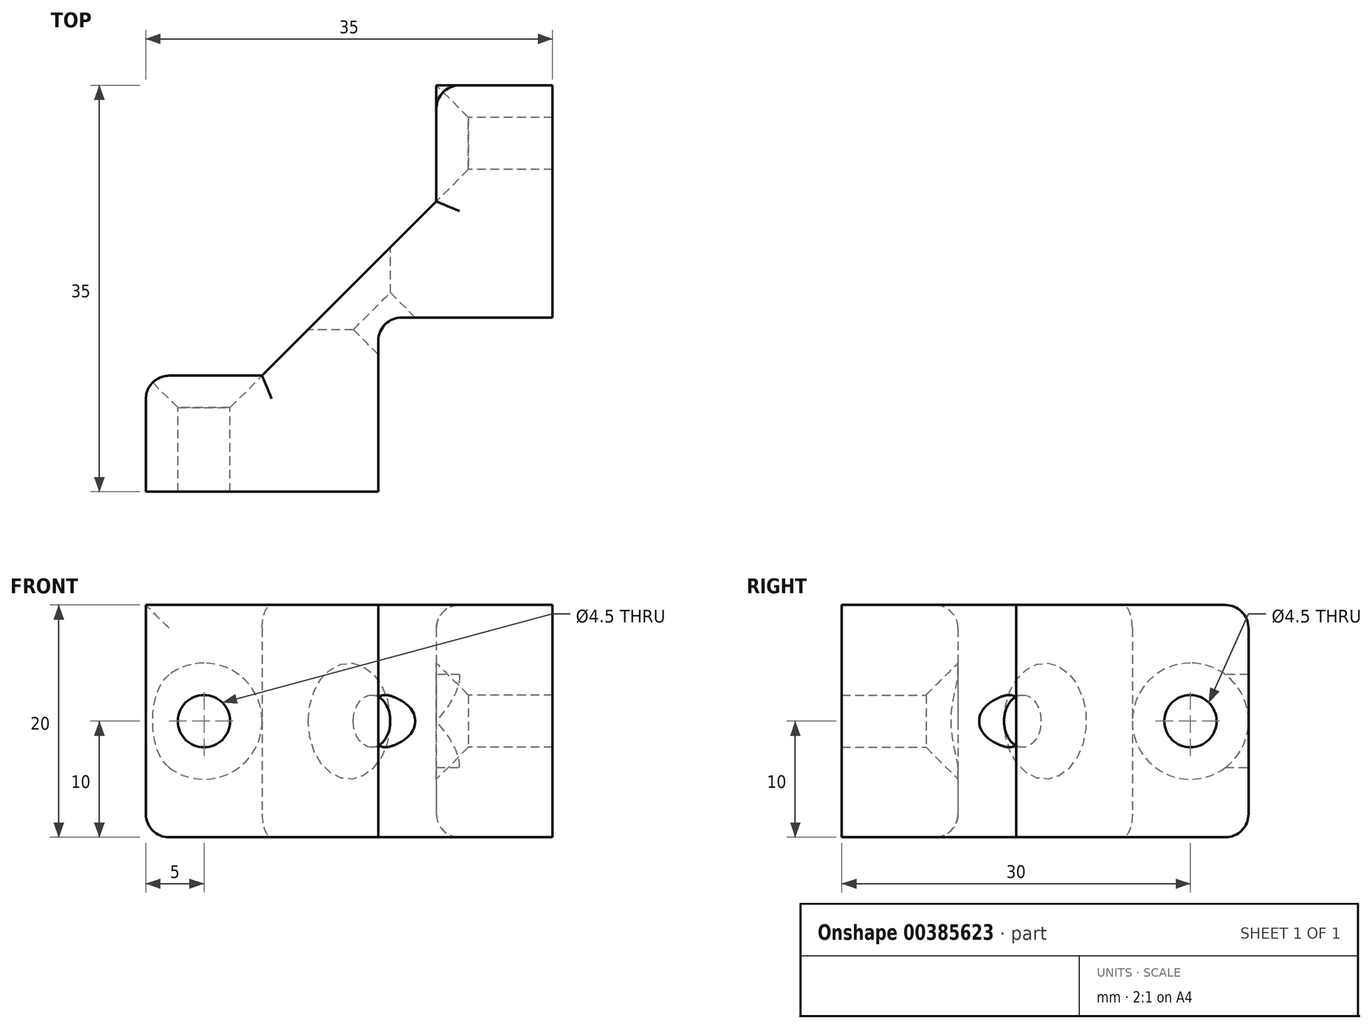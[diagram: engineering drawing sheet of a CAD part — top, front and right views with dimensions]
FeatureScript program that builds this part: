
annotation { "Feature Type Name" : "Feature", "Feature Type Description" : "" }
export const myFeature = defineFeature(function(context is Context, id is Id, definition is map)
    precondition{}
    {
        {
            var Q0;
            Q0=qCreatedBy(makeId("Top.planeOp"),FACE);
            var sketch = newSketch(context, id + "F0", { "sketchPlane" : qUnion([Q0])});
            skLineSegment(sketch, "E0", {"start": v(2, 0) * mm, "end": v(15, 0) * mm});
            skLineSegment(sketch, "E1", {"start": v(15, 0) * mm, "end": v(15, 20) * mm});
            skLineSegment(sketch, "E2", {"start": v(15, 20) * mm, "end": v(5, 20) * mm});
            skLineSegment(sketch, "E3", {"start": v(5, 20) * mm, "end": v(5, 10) * mm});
            skLineSegment(sketch, "E4", {"start": v(5, 10) * mm, "end": v(-10, -5) * mm});
            skLineSegment(sketch, "E5", {"start": v(-10, -5) * mm, "end": v(-20, -5) * mm});
            skLineSegment(sketch, "E6", {"start": v(-20, -5) * mm, "end": v(-20, -15) * mm});
            skLineSegment(sketch, "E7", {"start": v(-20, -15) * mm, "end": v(0, -15) * mm});
            skLineSegment(sketch, "E8", {"start": v(0, -15) * mm, "end": v(0, -2) * mm});
            skPoint(sketch, "E9.visualSharp", {"position": v(0, 0) * mm});
            skArc(sketch, "E9.filletArc", {"start": v(2, 0) * mm, "mid": v(0.59, -0.59) * mm, "end": v(0, -2) * mm});
            skSolve(sketch);
        }
        {
            var Q0;
            Q0 = qSketchRegion(id + "F0", true);
            extrude(context, id + "F1", {"entities" : qUnion([Q0]), "depth" : 20 * mm});
        }
        {
            var Q0;
            Q0=makeQuery(id+"F1.opExtrude","SWEPT_FACE",FACE,{"disambiguationData":[OSD([sQuery(id+"F0.wireOp",EDGE,"E5")])]});
            var sketch = newSketch(context, id + "F2", { "sketchPlane" : qUnion([Q0])});
            skCircle(sketch, "E10", {"center": v(15, 10) * mm, "radius": 2.5 * mm});
            skSolve(sketch);
        }
        {
            var Q0;
            Q0=sQuery(id+"F2.wireOp",VERTEX,"E10.center");
            var Q1;
            Q1=makeQuery(id+"F1.opExtrude","SWEPT_BODY",BODY,{"disambiguationData":[OSD([sQuery(id+"F0.wireOp",EDGE,"E0"),sQuery(id+"F0.wireOp",EDGE,"E1"),sQuery(id+"F0.wireOp",EDGE,"E2"),sQuery(id+"F0.wireOp",EDGE,"E3"),sQuery(id+"F0.wireOp",EDGE,"E4"),sQuery(id+"F0.wireOp",EDGE,"E5"),sQuery(id+"F0.wireOp",EDGE,"E6"),sQuery(id+"F0.wireOp",EDGE,"E7"),sQuery(id+"F0.wireOp",EDGE,"E8"),sQuery(id+"F0.wireOp",EDGE,"E9.filletArc")])]});
            hole(context, id + "F3", {"style" : HoleStyle.C_SINK, "endStyle" : HoleEndStyle.THROUGH, "holeDiameter" : 4.5 * mm, "cSinkDiameter" : 10 * mm, "cSinkAngle" : 90 * degree, "isTappedThrough" : true, "tappedDepth" : 12.7 * mm, "tapClearance" : 3, "startFromSketch" : true, "locations" : qUnion([Q0]), "scope" : qUnion([Q1])});
        }
        {
            var Q0;
            Q0=makeQuery(id+"F1.opExtrude","SWEPT_FACE",FACE,{"disambiguationData":[OSD([sQuery(id+"F0.wireOp",EDGE,"E3")])]});
            var sketch = newSketch(context, id + "F4", { "sketchPlane" : qUnion([Q0])});
            skCircle(sketch, "E11", {"center": v(-15, 10) * mm, "radius": 2 * mm});
            skSolve(sketch);
        }
        {
            var Q0;
            Q0=sQuery(id+"F4.wireOp",VERTEX,"E11.center");
            var Q1;
            Q1=makeQuery(id+"F1.opExtrude","SWEPT_BODY",BODY,{"disambiguationData":[OSD([sQuery(id+"F0.wireOp",EDGE,"E0"),sQuery(id+"F0.wireOp",EDGE,"E1"),sQuery(id+"F0.wireOp",EDGE,"E2"),sQuery(id+"F0.wireOp",EDGE,"E3"),sQuery(id+"F0.wireOp",EDGE,"E4"),sQuery(id+"F0.wireOp",EDGE,"E5"),sQuery(id+"F0.wireOp",EDGE,"E6"),sQuery(id+"F0.wireOp",EDGE,"E7"),sQuery(id+"F0.wireOp",EDGE,"E8"),sQuery(id+"F0.wireOp",EDGE,"E9.filletArc")])]});
            hole(context, id + "F5", {"style" : HoleStyle.C_SINK, "endStyle" : HoleEndStyle.THROUGH, "holeDiameter" : 4.5 * mm, "cSinkDiameter" : 10 * mm, "cSinkAngle" : 90 * degree, "isTappedThrough" : true, "tappedDepth" : 12.7 * mm, "tapClearance" : 3, "startFromSketch" : true, "locations" : qUnion([Q0]), "scope" : qUnion([Q1])});
        }
        {
            var Q0;
            Q0=makeQuery(id+"F1.opExtrude","CAP_EDGE",EDGE,{"disambiguationData":[OSD([sQuery(id+"F0.wireOp",EDGE,"E4")])],"isStart":false});
            fillet(context, id + "F6", {"entities" : qUnion([Q0]), "radius" : 2 * mm, "tangentPropagation" : true, "allowEdgeOverflow" : false});
        }
        {
            var Q0;
            Q0=makeQuery(id+"F1.opExtrude","CAP_EDGE",EDGE,{"disambiguationData":[OSD([sQuery(id+"F0.wireOp",EDGE,"E3")])],"isStart":false});
            fillet(context, id + "F7", {"entities" : qUnion([Q0]), "radius" : 2 * mm, "tangentPropagation" : true, "allowEdgeOverflow" : false});
        }
        {
            var Q0;
            Q0=makeQuery(id+"F1.opExtrude","CAP_EDGE",EDGE,{"disambiguationData":[OSD([sQuery(id+"F0.wireOp",EDGE,"E5")])],"isStart":false});
            fillet(context, id + "F8", {"entities" : qUnion([Q0]), "radius" : 2 * mm, "tangentPropagation" : true, "allowEdgeOverflow" : false});
        }
        {
            var Q0;
            Q0=makeQuery(id+"F1.opExtrude","CAP_EDGE",EDGE,{"disambiguationData":[OSD([sQuery(id+"F0.wireOp",EDGE,"E3")])],"isStart":true});
            fillet(context, id + "F9", {"entities" : qUnion([Q0]), "radius" : 2 * mm, "tangentPropagation" : true, "allowEdgeOverflow" : false});
        }
        {
            var Q0;
            Q0=makeQuery(id+"F1.opExtrude","CAP_EDGE",EDGE,{"disambiguationData":[OSD([sQuery(id+"F0.wireOp",EDGE,"E4")])],"isStart":true});
            var Q1;
            Q1=makeQuery(id+"F1.opExtrude","CAP_EDGE",EDGE,{"disambiguationData":[OSD([sQuery(id+"F0.wireOp",EDGE,"E5")])],"isStart":true});
            fillet(context, id + "F10", {"entities" : qUnion([Q0, Q1]), "radius" : 2 * mm, "tangentPropagation" : true, "allowEdgeOverflow" : false});
        }
        {
            var Q0;
            Q0=makeQuery(id+"F1.opExtrude","CAP_EDGE",EDGE,{"disambiguationData":[OSD([sQuery(id+"F0.wireOp",EDGE,"E6")])],"isStart":true});
            fillet(context, id + "F11", {"entities" : qUnion([Q0]), "radius" : 2 * mm, "tangentPropagation" : true, "allowEdgeOverflow" : false});
        }
        {
            var Q0;
            {var subQ0=sQuery(id+"F0.wireOp",EDGE,"E3");var subQ1=sQuery(id+"F0.wireOp",EDGE,"E2");Q0=makeQuery(id+"F5.hole-0.boolean.opBoolean","SPLIT",EDGE,{"disambiguationData":[TD([makeQuery(id+"F1.opExtrude","CAP_FACE",FACE,{"disambiguationData":[OSD([sQuery(id+"F0.wireOp",EDGE,"E0"),sQuery(id+"F0.wireOp",EDGE,"E1"),subQ1,subQ0,sQuery(id+"F0.wireOp",EDGE,"E4"),sQuery(id+"F0.wireOp",EDGE,"E5"),sQuery(id+"F0.wireOp",EDGE,"E6"),sQuery(id+"F0.wireOp",EDGE,"E7"),sQuery(id+"F0.wireOp",EDGE,"E8"),sQuery(id+"F0.wireOp",EDGE,"E9.filletArc")])],"isStart":false})])],"derivedFrom":makeQuery(id+"F1.opExtrude","SWEPT_EDGE",EDGE,{"disambiguationData":[OSD([subQ1,subQ0])]})});}
            fillet(context, id + "F12", {"entities" : qUnion([Q0]), "radius" : 2 * mm, "tangentPropagation" : true, "allowEdgeOverflow" : false});
        }
        {
            var Q0;
            Q0=makeQuery(id+"F1.opExtrude","SWEPT_FACE",FACE,{"disambiguationData":[OSD([sQuery(id+"F0.wireOp",EDGE,"E4")])]});
            var sketch = newSketch(context, id + "F13", { "sketchPlane" : qUnion([Q0])});
            skSolve(sketch);
        }
        {
            var Q0;
            {var subQ5=sQuery(id+"F0.wireOp",EDGE,"E4");var subQ11=makeQuery(id+"F1.opExtrude","SWEPT_FACE",FACE,{"disambiguationData":[OSD([subQ5])]});Q0=makeQuery(id+"F13.imprint","IMPRINT",FACE,{"disambiguationData":[TD([[makeQuery(id+"F13.imprint","IMPRINT",EDGE,{"derivedFrom":makeQuery(id+"F6.opFillet","BLEND_EDGE",EDGE,{"blendedFrom":[makeQuery(id+"F1.opExtrude","CAP_EDGE",EDGE,{"disambiguationData":[OSD([subQ5])],"isStart":false}),subQ11],"blendedInto":[subQ11]})}),1.0]])]});}
            var sketch = newSketch(context, id + "F14", { "sketchPlane" : qUnion([Q0])});
            skCircle(sketch, "E12", {"center": v(0, 10) * mm, "radius": 2.86 * mm});
            skSolve(sketch);
        }
        {
            var Q0;
            Q0=sQuery(id+"F14.wireOp",VERTEX,"E12.center");
            var Q1;
            Q1=makeQuery(id+"F1.opExtrude","SWEPT_BODY",BODY,{"disambiguationData":[OSD([sQuery(id+"F0.wireOp",EDGE,"E0"),sQuery(id+"F0.wireOp",EDGE,"E1"),sQuery(id+"F0.wireOp",EDGE,"E2"),sQuery(id+"F0.wireOp",EDGE,"E3"),sQuery(id+"F0.wireOp",EDGE,"E4"),sQuery(id+"F0.wireOp",EDGE,"E5"),sQuery(id+"F0.wireOp",EDGE,"E6"),sQuery(id+"F0.wireOp",EDGE,"E7"),sQuery(id+"F0.wireOp",EDGE,"E8"),sQuery(id+"F0.wireOp",EDGE,"E9.filletArc")])]});
            hole(context, id + "F15", {"style" : HoleStyle.C_SINK, "endStyle" : HoleEndStyle.THROUGH, "holeDiameter" : 4.5 * mm, "cSinkDiameter" : 10 * mm, "cSinkAngle" : 90 * degree, "isTappedThrough" : true, "tappedDepth" : 12.7 * mm, "tapClearance" : 3, "startFromSketch" : true, "locations" : qUnion([Q0]), "scope" : qUnion([Q1])});
        }
    });
